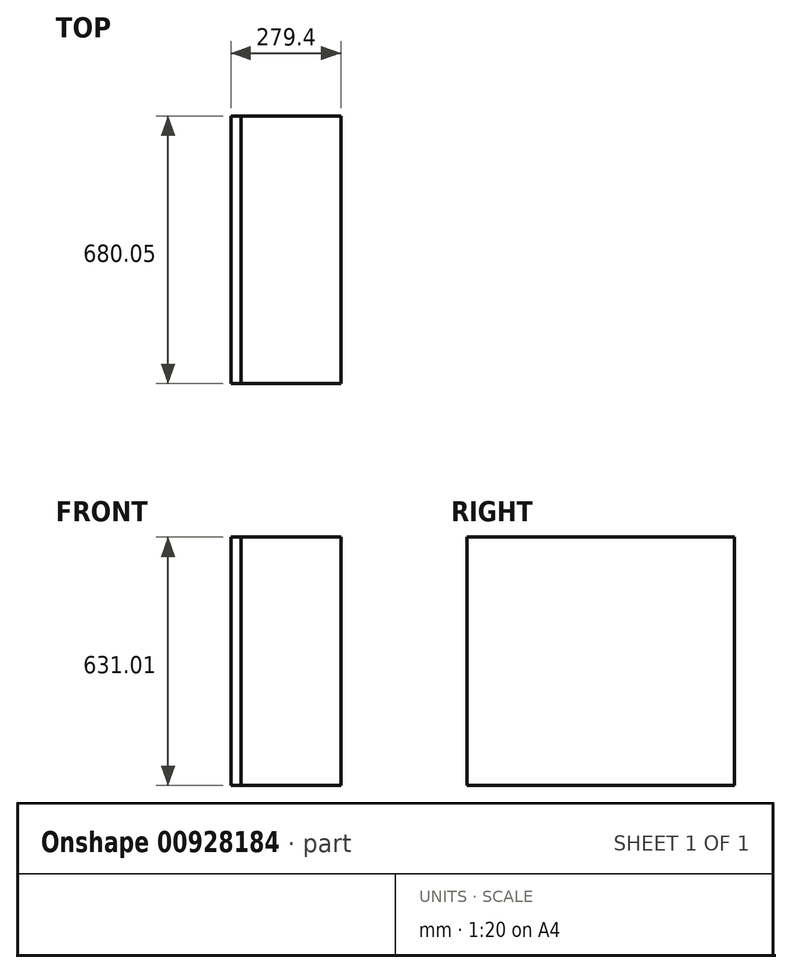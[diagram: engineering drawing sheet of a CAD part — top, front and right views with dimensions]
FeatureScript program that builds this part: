
annotation { "Feature Type Name" : "Feature", "Feature Type Description" : "" }
export const myFeature = defineFeature(function(context is Context, id is Id, definition is map)
    precondition{}
    {
        {
            var Q0;
            Q0=qCreatedBy(makeId("Right.planeOp"),FACE);
            var sketch = newSketch(context, id + "F0", { "sketchPlane" : qUnion([Q0])});
            skLineSegment(sketch, "E0.bottom", {"start": v(-147.15, -282.2) * mm, "end": v(-827.2, -282.2) * mm});
            skLineSegment(sketch, "E0.top", {"start": v(-147.15, -913.22) * mm, "end": v(-827.2, -913.22) * mm});
            skLineSegment(sketch, "E0.left", {"start": v(-147.15, -282.2) * mm, "end": v(-147.15, -913.22) * mm});
            skLineSegment(sketch, "E0.right", {"start": v(-827.2, -282.2) * mm, "end": v(-827.2, -913.22) * mm});
            skSolve(sketch);
        }
        {
            var Q0;
            Q0=makeQuery(id+"F0.imprint","IMPRINT",FACE,{"disambiguationData":[TD([[makeQuery(id+"F0.imprint","IMPRINT",EDGE,{"derivedFrom":sQuery(id+"F0.wireOp",EDGE,"E0.bottom")}),1.0]])]});
            extrude(context, id + "F1", {"entities" : qUnion([Q0]), "depth" : 25.4 * mm, "offsetDistance" : 25.4 * mm});
        }
        {
            var Q0;
            Q0=makeQuery(id+"F1.opExtrude","CAP_FACE",FACE,{"disambiguationData":[OSD([sQuery(id+"F0.wireOp",EDGE,"E0.bottom"),sQuery(id+"F0.wireOp",EDGE,"E0.top"),sQuery(id+"F0.wireOp",EDGE,"E0.left"),sQuery(id+"F0.wireOp",EDGE,"E0.right")])],"isStart":false});
            extrude(context, id + "F2", {"entities" : qUnion([Q0]), "depth" : 254 * mm, "offsetDistance" : 25.4 * mm});
        }
    });
